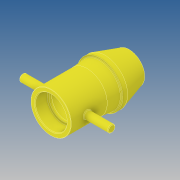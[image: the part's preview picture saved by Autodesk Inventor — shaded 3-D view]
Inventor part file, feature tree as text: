
AUTODESK INVENTOR PART (.ipt)
format: ipt  version: 2019 (Build 230136000, 136)  size: 182,784 bytes
history: native  units: mm
features: other x2, sketch x2, extrude x1, chamfer x1, pattern_circular x1
ambient origin geometry x8: Origin, YZ Plane, XZ Plane, XY Plane, X Axis, Y Axis, Z Axis, Center Point
bodies: Solide1 (feature_tree)
feature tree (7):
  other  "Révolution1"
  other  "Plan de construction1"
  extrude  "Extrusion1"  Depth=0.25mm
  chamfer  "Chanfrein1"  Distance=0.25mm
  pattern_circular  "Réseau circulaire1"  Angle=90.0deg  [1 undecoded]
  sketch  "Esquisse1"
  sketch  "Esquisse2"
note: 1 required parameter value undecoded (feature->parameter linkage not recoverable at this tier; creation-order binding heuristic only, values carry confidence <= 0.55)
